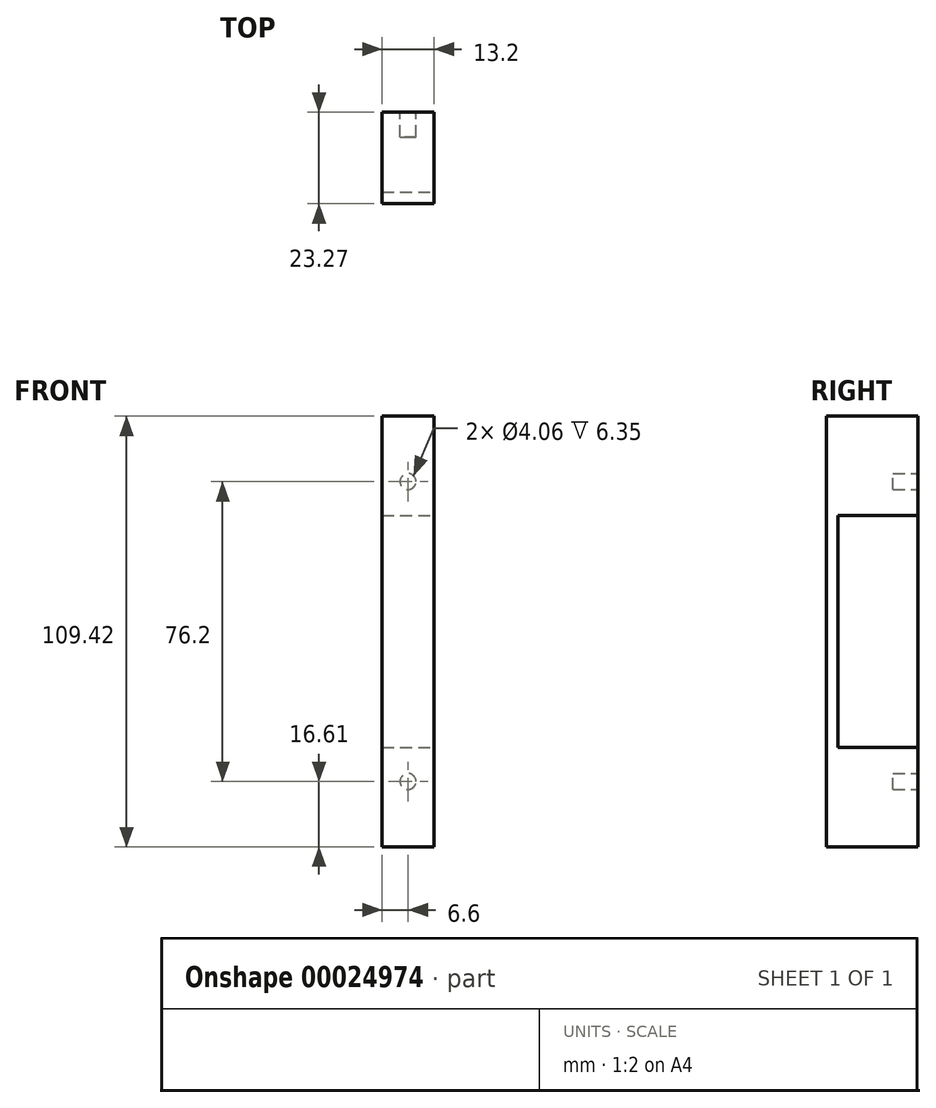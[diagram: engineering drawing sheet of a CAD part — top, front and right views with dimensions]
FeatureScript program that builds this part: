
annotation { "Feature Type Name" : "Feature", "Feature Type Description" : "" }
export const myFeature = defineFeature(function(context is Context, id is Id, definition is map)
    precondition{}
    {
        {
            var Q0;
            Q0=qCreatedBy(makeId("Front.planeOp"),FACE);
            var sketch = newSketch(context, id + "F0", { "sketchPlane" : qUnion([Q0])});
            skLineSegment(sketch, "E0.bottom", {"start": v(-6.6, 54.71) * mm, "end": v(6.6, 54.71) * mm});
            skLineSegment(sketch, "E0.top", {"start": v(-6.6, -54.71) * mm, "end": v(6.6, -54.71) * mm});
            skLineSegment(sketch, "E0.left", {"start": v(-6.6, 54.71) * mm, "end": v(-6.6, -54.71) * mm});
            skLineSegment(sketch, "E0.right", {"start": v(6.6, 54.71) * mm, "end": v(6.6, -54.71) * mm});
            skLineSegment(sketch, "E1.bottom", {"start": v(-6.6, 29.45) * mm, "end": v(6.6, 29.45) * mm});
            skLineSegment(sketch, "E1.top", {"start": v(-6.6, -29.45) * mm, "end": v(6.6, -29.45) * mm});
            skLineSegment(sketch, "E1.left", {"start": v(-6.6, 29.45) * mm, "end": v(-6.6, -29.45) * mm});
            skLineSegment(sketch, "E1.right", {"start": v(6.6, 29.45) * mm, "end": v(6.6, -29.45) * mm});
            skCircle(sketch, "E2", {"center": v(0, 38.1) * mm, "radius": 2.03 * mm});
            skCircle(sketch, "E3", {"center": v(0, -38.1) * mm, "radius": 2.03 * mm});
            skPoint(sketch, "E4", {"position": v(0, 0) * mm});
            skSolve(sketch);
        }
        {
            var Q0;
            Q0=makeQuery(id+"F0.imprint","IMPRINT",FACE,{"disambiguationData":[TD([[makeQuery(id+"F0.imprint","IMPRINT",EDGE,{"derivedFrom":sQuery(id+"F0.wireOp",EDGE,"E2")}),1.0]])]});
            var Q1;
            Q1=makeQuery(id+"F0.imprint","IMPRINT",FACE,{"disambiguationData":[TD([[makeQuery(id+"F0.imprint","IMPRINT",EDGE,{"derivedFrom":sQuery(id+"F0.wireOp",EDGE,"E3")}),1.0]])]});
            var Q2;
            {var subQ2=sQuery(id+"F0.wireOp",EDGE,"E0.bottom");Q2=makeQuery(id+"F0.imprint","IMPRINT",FACE,{"disambiguationData":[TD([[makeQuery(id+"F0.imprint","IMPRINT",EDGE,{"derivedFrom":subQ2}),-1.0]])]});}
            var Q3;
            {var subQ2=sQuery(id+"F0.wireOp",EDGE,"E0.top");Q3=makeQuery(id+"F0.imprint","IMPRINT",FACE,{"disambiguationData":[TD([[makeQuery(id+"F0.imprint","IMPRINT",EDGE,{"derivedFrom":subQ2}),1.0]])]});}
            var Q4;
            Q4=makeQuery(id+"F0.imprint","IMPRINT",FACE,{"disambiguationData":[TD([[makeQuery(id+"F0.imprint","IMPRINT",EDGE,{"derivedFrom":sQuery(id+"F0.wireOp",EDGE,"E1.bottom")}),-1.0]])]});
            extrude(context, id + "F1", {"entities" : qUnion([Q0, Q1, Q2, Q3, Q4]), "depth" : 23.27 * mm});
        }
        {
            var Q0;
            Q0=makeQuery(id+"F0.imprint","IMPRINT",FACE,{"disambiguationData":[TD([[makeQuery(id+"F0.imprint","IMPRINT",EDGE,{"derivedFrom":sQuery(id+"F0.wireOp",EDGE,"E1.bottom")}),-1.0]])]});
            extrude(context, id + "F2", {"entities" : qUnion([Q0]), "depth" : 20.32 * mm});
        }
        {
            var Q0;
            Q0=makeQuery(id+"F2.opExtrude","SWEPT_BODY",BODY,{"disambiguationData":[OSD([sQuery(id+"F0.wireOp",EDGE,"E1.bottom"),sQuery(id+"F0.wireOp",EDGE,"E1.top"),sQuery(id+"F0.wireOp",EDGE,"E1.left"),sQuery(id+"F0.wireOp",EDGE,"E1.right")])]});
            var Q1;
            Q1=makeQuery(id+"F1.opExtrude","SWEPT_BODY",BODY,{"disambiguationData":[OSD([sQuery(id+"F0.wireOp",EDGE,"E0.bottom"),sQuery(id+"F0.wireOp",EDGE,"E0.top"),sQuery(id+"F0.wireOp",EDGE,"E0.left"),sQuery(id+"F0.wireOp",EDGE,"E0.right"),sQuery(id+"F0.wireOp",EDGE,"E1.left"),sQuery(id+"F0.wireOp",EDGE,"E1.right")])]});
            booleanBodies(context, id + "F3", {"operationType" : BooleanOperationType.SUBTRACTION, "tools" : qUnion([Q0]), "targets" : qUnion([Q1]), "keepTools" : true});
        }
        {
            var Q0;
            Q0=makeQuery(id+"F0.imprint","IMPRINT",FACE,{"disambiguationData":[TD([[makeQuery(id+"F0.imprint","IMPRINT",EDGE,{"derivedFrom":sQuery(id+"F0.wireOp",EDGE,"E2")}),1.0]])]});
            var Q1;
            Q1=makeQuery(id+"F0.imprint","IMPRINT",FACE,{"disambiguationData":[TD([[makeQuery(id+"F0.imprint","IMPRINT",EDGE,{"derivedFrom":sQuery(id+"F0.wireOp",EDGE,"E3")}),1.0]])]});
            extrude(context, id + "F4", {"entities" : qUnion([Q0, Q1]), "depth" : 6.35 * mm});
        }
        {
            var Q0;
            Q0=makeQuery(id+"F4.opExtrude","SWEPT_BODY",BODY,{"disambiguationData":[OSD([sQuery(id+"F0.wireOp",EDGE,"E2")])]});
            var Q1;
            Q1=makeQuery(id+"F4.opExtrude","SWEPT_BODY",BODY,{"disambiguationData":[OSD([sQuery(id+"F0.wireOp",EDGE,"E3")])]});
            var Q2;
            Q2=makeQuery(id+"F1.opExtrude","SWEPT_BODY",BODY,{"disambiguationData":[OSD([sQuery(id+"F0.wireOp",EDGE,"E0.bottom"),sQuery(id+"F0.wireOp",EDGE,"E0.top"),sQuery(id+"F0.wireOp",EDGE,"E0.left"),sQuery(id+"F0.wireOp",EDGE,"E0.right"),sQuery(id+"F0.wireOp",EDGE,"E1.left"),sQuery(id+"F0.wireOp",EDGE,"E1.right")])]});
            booleanBodies(context, id + "F5", {"operationType" : BooleanOperationType.SUBTRACTION, "tools" : qUnion([Q0, Q1]), "targets" : qUnion([Q2]), "keepTools" : true});
        }
    });
